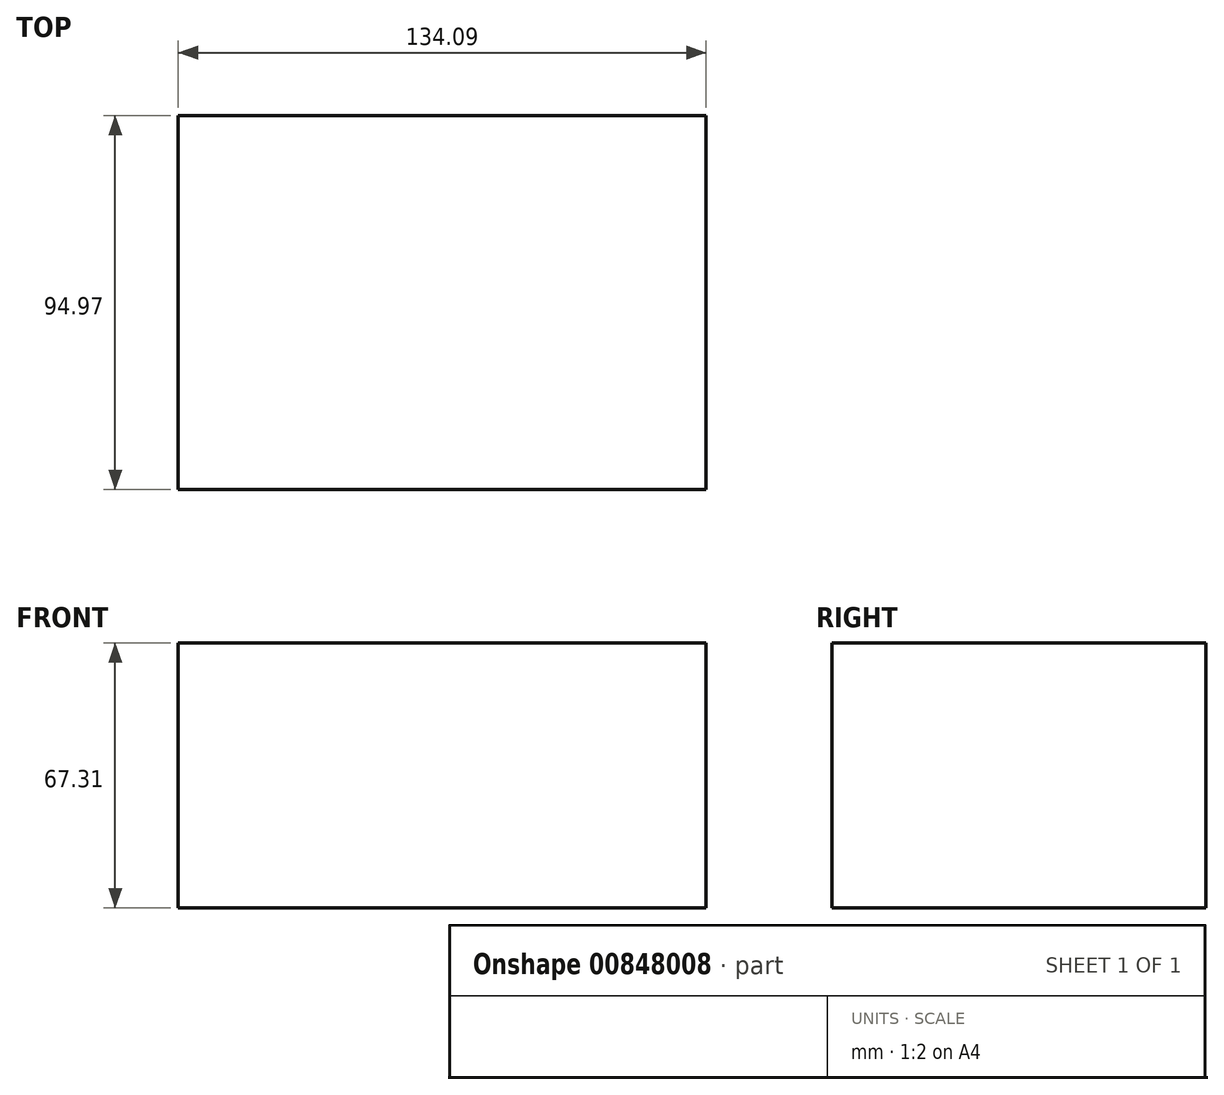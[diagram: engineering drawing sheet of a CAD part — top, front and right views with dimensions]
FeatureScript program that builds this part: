
annotation { "Feature Type Name" : "Feature", "Feature Type Description" : "" }
export const myFeature = defineFeature(function(context is Context, id is Id, definition is map)
    precondition{}
    {
        {
            var Q0;
            Q0=qCreatedBy(makeId("Top.planeOp"),FACE);
            var sketch = newSketch(context, id + "F0", { "sketchPlane" : qUnion([Q0])});
            skLineSegment(sketch, "E0.bottom", {"start": v(-60.01, 0) * mm, "end": v(74.08, 0) * mm});
            skLineSegment(sketch, "E0.top", {"start": v(-60.01, 94.97) * mm, "end": v(74.08, 94.97) * mm});
            skLineSegment(sketch, "E0.left", {"start": v(-60.01, 0) * mm, "end": v(-60.01, 94.97) * mm});
            skLineSegment(sketch, "E0.right", {"start": v(74.08, 0) * mm, "end": v(74.08, 94.97) * mm});
            skSolve(sketch);
        }
        {
            var Q0;
            Q0=makeQuery(id+"F0.imprint","IMPRINT",FACE,{"disambiguationData":[TD([[makeQuery(id+"F0.imprint","IMPRINT",EDGE,{"derivedFrom":sQuery(id+"F0.wireOp",EDGE,"E0.bottom")}),1.0]])]});
            extrude(context, id + "F1", {"entities" : qUnion([Q0]), "depth" : 67.3 * mm, "offsetDistance" : 25 * mm});
        }
    });
